# Revit family: Lighting_Fixture-Ceiling-Astro-Mantova
name_source: partatom
category: Lighting Fixtures
revit_build: Autodesk Revit 2014 (Build: 20130308_1515(x64)
units: mm (PartAtom-declared; Revit-internal decimal feet)

## types (1)
- 7274 Mantova
    Apparent Load = 18 VA
    Assembly Code = D5020200
    Casing Material = Astro - Steel - White
    Class = 2
    Color Filter = 16777215
    Default Elevation = 1219.2 mm  [stored 4 ft]
    Description = Ceiling light
    Dimmable = No
    Dimming Lamp Color Temperature Shift = <None>
    Energy Efficiency Rating = A++
    Height = 81 mm  [stored 0.265748 ft]
    IP Rating = IP44
    Lamp = LED
    Lamp included = Yes
    Length = 350 mm  [stored 1.14829 ft]
    Light Source Elevation = 30 mm  [stored 0.0984252 ft]
    Luminaire Lamp Efficiency Rating = A++
    Manufacturer = Astro Lighting Ltd, CM20 2DP
    Model = 7274 Mantova
    Mountable on normally flammable surfaces = Yes
    Number of Poles = 1
    Photometric Web File = Astro P4558 PV Mantova  261114.IES
    Product Documentation = http://www.astrolighting.co.uk
    Suitable for bathroom zone = Zone 2, 3
    Tilt Angle = -90.00°
    Type Comments = -Includes integral LED driver, -For ceiling use only
    URL = www.astrolighting.co.uk
    Voltage = 230 V
    Wattage Comments = 17.7w
    Weight = 2.37kg
    Width = 350 mm  [stored 1.14829 ft]

note: [stored X ft] marks values corroborated as IEEE doubles in the binary element streams (Revit-internal decimal feet)

## geometry (parser evidence)
native form markers: Sweep x1
no freeform markers — native parametric forms only
